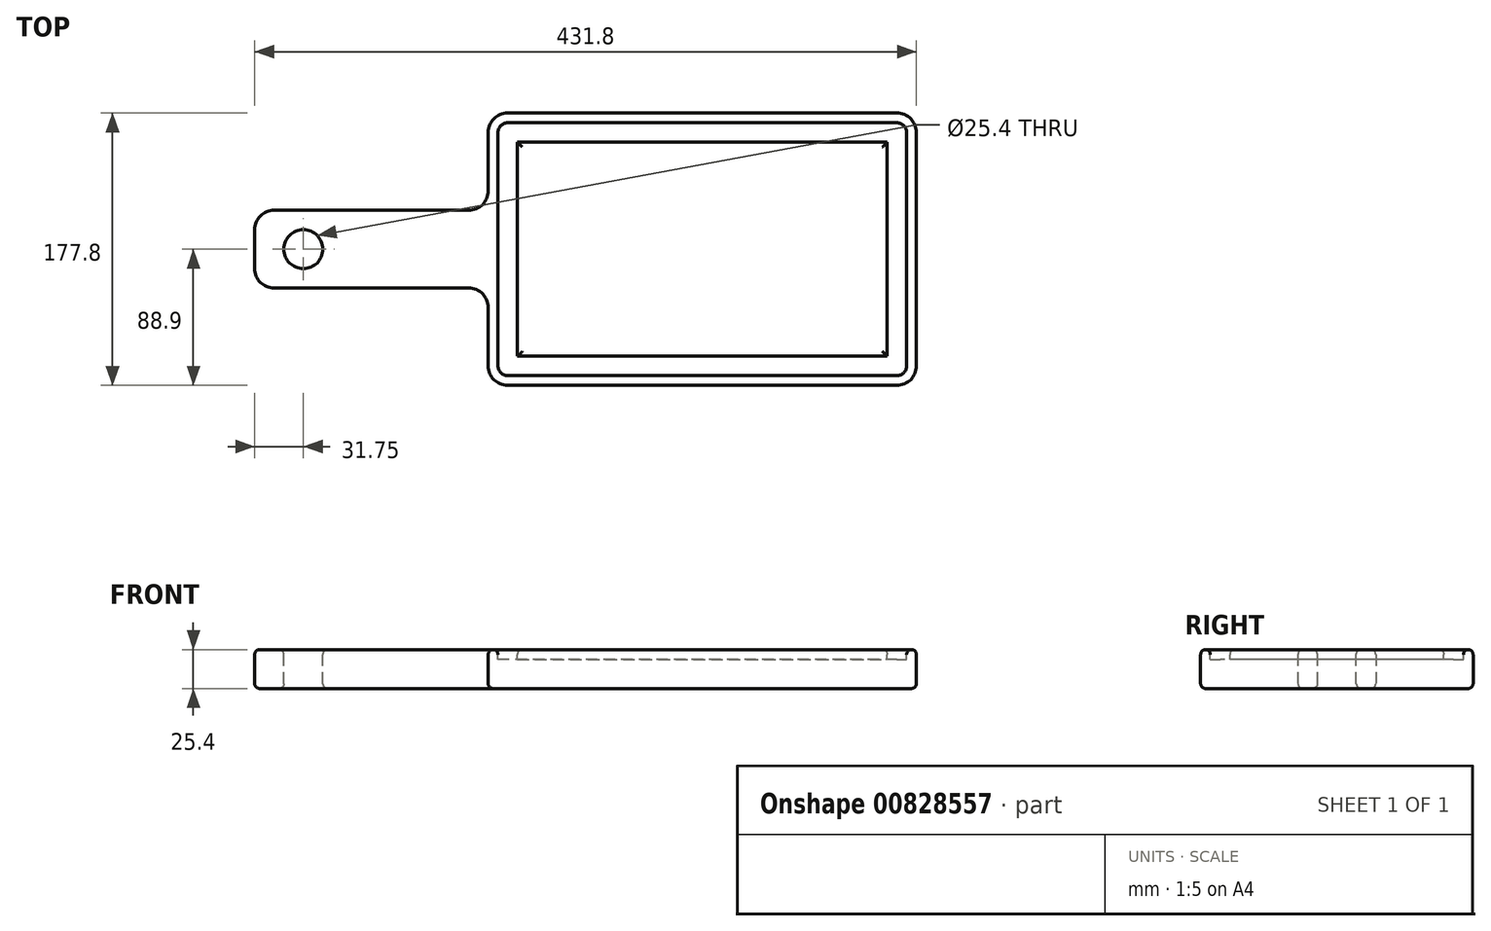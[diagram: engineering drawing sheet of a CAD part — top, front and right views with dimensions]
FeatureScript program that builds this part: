
annotation { "Feature Type Name" : "Feature", "Feature Type Description" : "" }
export const myFeature = defineFeature(function(context is Context, id is Id, definition is map)
    precondition{}
    {
        {
            var Q0;
            Q0=qCreatedBy(makeId("Top.planeOp"),FACE);
            var sketch = newSketch(context, id + "F0", { "sketchPlane" : qUnion([Q0])});
            skLineSegment(sketch, "E0.bottom", {"start": v(0, 0) * mm, "end": v(279.4, 0) * mm});
            skLineSegment(sketch, "E0.top", {"start": v(0, 177.8) * mm, "end": v(279.4, 177.8) * mm});
            skLineSegment(sketch, "E0.left", {"start": v(0, 0) * mm, "end": v(0, 177.8) * mm});
            skLineSegment(sketch, "E0.right", {"start": v(279.4, 0) * mm, "end": v(279.4, 177.8) * mm});
            skLineSegment(sketch, "E1.bottom", {"start": v(0, 114.3) * mm, "end": v(-152.4, 114.3) * mm});
            skLineSegment(sketch, "E1.top", {"start": v(0, 63.5) * mm, "end": v(-152.4, 63.5) * mm});
            skLineSegment(sketch, "E1.left", {"start": v(0, 114.3) * mm, "end": v(0, 63.5) * mm});
            skLineSegment(sketch, "E1.right", {"start": v(-152.4, 114.3) * mm, "end": v(-152.4, 63.5) * mm});
            skSolve(sketch);
        }
        {
            var Q0;
            {var subQ3=sQuery(id+"F0.wireOp",EDGE,"E0.bottom");Q0=makeQuery(id+"F0.imprint","IMPRINT",FACE,{"disambiguationData":[TD([[makeQuery(id+"F0.imprint","IMPRINT",EDGE,{"derivedFrom":subQ3}),1.0]])]});}
            var Q1;
            Q1=makeQuery(id+"F0.imprint","IMPRINT",FACE,{"disambiguationData":[TD([[makeQuery(id+"F0.imprint","IMPRINT",EDGE,{"derivedFrom":sQuery(id+"F0.wireOp",EDGE,"E1.bottom")}),1.0]])]});
            extrude(context, id + "F1", {"entities" : qUnion([Q0, Q1]), "depth" : 25.4 * mm, "offsetDistance" : 25.4 * mm});
        }
        {
            var Q0;
            Q0=makeQuery(id+"F1.opExtrude","CAP_FACE",FACE,{"disambiguationData":[OSD([sQuery(id+"F0.wireOp",EDGE,"E0.bottom"),sQuery(id+"F0.wireOp",EDGE,"E0.top"),sQuery(id+"F0.wireOp",EDGE,"E0.left"),sQuery(id+"F0.wireOp",EDGE,"E0.right"),sQuery(id+"F0.wireOp",EDGE,"E1.bottom"),sQuery(id+"F0.wireOp",EDGE,"E1.top"),sQuery(id+"F0.wireOp",EDGE,"E1.right")])],"isStart":false});
            var sketch = newSketch(context, id + "F2", { "sketchPlane" : qUnion([Q0])});
            skCircle(sketch, "E2", {"center": v(-120.65, 88.9) * mm, "radius": 12.7 * mm});
            skSolve(sketch);
        }
        {
            var Q0;
            Q0 = qSketchRegion(id + "F2", true);
            extrude(context, id + "F3", {"entities" : qUnion([Q0]), "operationType" : NewBodyOperationType.REMOVE, "oppositeDirection" : true, "depth" : 25.4 * mm, "offsetDistance" : 25.4 * mm});
        }
        {
            var Q0;
            Q0=makeQuery(id+"F1.opExtrude","CAP_FACE",FACE,{"disambiguationData":[OSD([sQuery(id+"F0.wireOp",EDGE,"E0.bottom"),sQuery(id+"F0.wireOp",EDGE,"E0.top"),sQuery(id+"F0.wireOp",EDGE,"E0.left"),sQuery(id+"F0.wireOp",EDGE,"E0.right"),sQuery(id+"F0.wireOp",EDGE,"E1.bottom"),sQuery(id+"F0.wireOp",EDGE,"E1.top"),sQuery(id+"F0.wireOp",EDGE,"E1.right")])],"isStart":false});
            var sketch = newSketch(context, id + "F4", { "sketchPlane" : qUnion([Q0])});
            skLineSegment(sketch, "E3.0", {"start": v(6.35, 177.8) * mm, "end": v(279.4, 177.8) * mm});
            skLineSegment(sketch, "E4.0", {"start": v(273.05, 171.45) * mm, "end": v(6.35, 171.45) * mm});
            skLineSegment(sketch, "E4.1", {"start": v(273.05, 6.35) * mm, "end": v(273.05, 171.45) * mm});
            skLineSegment(sketch, "E4.2", {"start": v(6.35, 171.45) * mm, "end": v(6.35, 107.95) * mm});
            skLineSegment(sketch, "E4.3", {"start": v(6.35, 6.35) * mm, "end": v(273.05, 6.35) * mm});
            skLineSegment(sketch, "E4.4", {"start": v(6.35, 107.95) * mm, "end": v(-146.05, 107.95) * mm});
            skLineSegment(sketch, "E4.5", {"start": v(-146.05, 107.95) * mm, "end": v(-146.05, 69.85) * mm});
            skLineSegment(sketch, "E4.6", {"start": v(-146.05, 69.85) * mm, "end": v(6.35, 69.85) * mm});
            skLineSegment(sketch, "E4.7", {"start": v(6.35, 69.85) * mm, "end": v(6.35, 6.35) * mm});
            skLineSegment(sketch, "E5.0", {"start": v(273.05, 184.15) * mm, "end": v(6.35, 184.15) * mm});
            skLineSegment(sketch, "E6", {"start": v(6.35, 107.95) * mm, "end": v(6.35, 69.85) * mm});
            skLineSegment(sketch, "E7.0", {"start": v(19.05, 158.75) * mm, "end": v(19.05, 107.95) * mm});
            skLineSegment(sketch, "E7.1", {"start": v(19.05, 69.85) * mm, "end": v(19.05, 19.05) * mm});
            skLineSegment(sketch, "E7.2", {"start": v(19.05, 19.05) * mm, "end": v(260.35, 19.05) * mm});
            skLineSegment(sketch, "E7.3", {"start": v(260.35, 19.05) * mm, "end": v(260.35, 158.75) * mm});
            skLineSegment(sketch, "E7.4", {"start": v(260.35, 158.75) * mm, "end": v(19.05, 158.75) * mm});
            skLineSegment(sketch, "E8", {"start": v(19.05, 107.95) * mm, "end": v(19.05, 69.85) * mm});
            skSolve(sketch);
        }
        {
            var Q0;
            Q0=makeQuery(id+"F4.imprint","IMPRINT",FACE,{"disambiguationData":[TD([[makeQuery(id+"F4.imprint","IMPRINT",EDGE,{"derivedFrom":sQuery(id+"F4.wireOp",EDGE,"E4.0")}),1.0]])]});
            extrude(context, id + "F5", {"entities" : qUnion([Q0]), "operationType" : NewBodyOperationType.REMOVE, "oppositeDirection" : true, "depth" : 6.35 * mm, "offsetDistance" : 25.4 * mm});
        }
        {
            var Q0;
            Q0=makeQuery(id+"F5.boolean.opBoolean","COPY",EDGE,{"derivedFrom":makeQuery(id+"F5.opExtrude","SWEPT_EDGE",EDGE,{"disambiguationData":[OSD([sQuery(id+"F4.wireOp",EDGE,"E4.0"),sQuery(id+"F4.wireOp",EDGE,"E4.2")])]})});
            var Q1;
            Q1=makeQuery(id+"F5.boolean.opBoolean","COPY",EDGE,{"derivedFrom":makeQuery(id+"F5.opExtrude","SWEPT_EDGE",EDGE,{"disambiguationData":[OSD([sQuery(id+"F4.wireOp",EDGE,"E4.0"),sQuery(id+"F4.wireOp",EDGE,"E4.1")])]})});
            var Q2;
            Q2=makeQuery(id+"F5.boolean.opBoolean","COPY",EDGE,{"derivedFrom":makeQuery(id+"F5.opExtrude","SWEPT_EDGE",EDGE,{"disambiguationData":[OSD([sQuery(id+"F4.wireOp",EDGE,"E4.3"),sQuery(id+"F4.wireOp",EDGE,"E4.7")])]})});
            var Q3;
            Q3=makeQuery(id+"F5.boolean.opBoolean","COPY",EDGE,{"derivedFrom":makeQuery(id+"F5.opExtrude","SWEPT_EDGE",EDGE,{"disambiguationData":[OSD([sQuery(id+"F4.wireOp",EDGE,"E4.1"),sQuery(id+"F4.wireOp",EDGE,"E4.3")])]})});
            fillet(context, id + "F6", {"entities" : qUnion([Q0, Q1, Q2, Q3]), "radius" : 6.35 * mm, "tangentPropagation" : true, "allowEdgeOverflow" : false});
        }
        {
            var Q0;
            Q0=makeQuery(id+"F1.opExtrude","SWEPT_EDGE",EDGE,{"disambiguationData":[OSD([sQuery(id+"F0.wireOp",EDGE,"E0.bottom"),sQuery(id+"F0.wireOp",EDGE,"E0.left")])]});
            var Q1;
            Q1=makeQuery(id+"F1.opExtrude","SWEPT_EDGE",EDGE,{"disambiguationData":[OSD([sQuery(id+"F0.wireOp",EDGE,"E1.top"),sQuery(id+"F0.wireOp",EDGE,"E1.right")])]});
            var Q2;
            Q2=makeQuery(id+"F1.opExtrude","SWEPT_EDGE",EDGE,{"disambiguationData":[OSD([sQuery(id+"F0.wireOp",EDGE,"E0.left"),sQuery(id+"F0.wireOp",EDGE,"E1.top"),sQuery(id+"F0.wireOp",EDGE,"E1.left")])]});
            var Q3;
            Q3=makeQuery(id+"F1.opExtrude","SWEPT_EDGE",EDGE,{"disambiguationData":[OSD([sQuery(id+"F0.wireOp",EDGE,"E1.bottom"),sQuery(id+"F0.wireOp",EDGE,"E1.right")])]});
            var Q4;
            Q4=makeQuery(id+"F1.opExtrude","SWEPT_EDGE",EDGE,{"disambiguationData":[OSD([sQuery(id+"F0.wireOp",EDGE,"E0.left"),sQuery(id+"F0.wireOp",EDGE,"E1.bottom"),sQuery(id+"F0.wireOp",EDGE,"E1.left")])]});
            var Q5;
            Q5=makeQuery(id+"F1.opExtrude","SWEPT_EDGE",EDGE,{"disambiguationData":[OSD([sQuery(id+"F0.wireOp",EDGE,"E0.top"),sQuery(id+"F0.wireOp",EDGE,"E0.left")])]});
            var Q6;
            Q6=makeQuery(id+"F1.opExtrude","SWEPT_EDGE",EDGE,{"disambiguationData":[OSD([sQuery(id+"F0.wireOp",EDGE,"E0.bottom"),sQuery(id+"F0.wireOp",EDGE,"E0.right")])]});
            var Q7;
            Q7=makeQuery(id+"F1.opExtrude","SWEPT_EDGE",EDGE,{"disambiguationData":[OSD([sQuery(id+"F0.wireOp",EDGE,"E0.top"),sQuery(id+"F0.wireOp",EDGE,"E0.right")])]});
            fillet(context, id + "F7", {"entities" : qUnion([Q0, Q1, Q2, Q3, Q4, Q5, Q6, Q7]), "radius" : 12.7 * mm, "tangentPropagation" : true, "allowEdgeOverflow" : false});
        }
        {
            var Q0;
            Q0=makeQuery(id+"F5.boolean.opBoolean","SPLIT",FACE,{"disambiguationData":[TD([makeQuery(id+"F5.opExtrude","SWEPT_FACE",FACE,{"disambiguationData":[OSD([sQuery(id+"F4.wireOp",EDGE,"E7.2")])]})])],"derivedFrom":makeQuery(id+"F1.opExtrude","CAP_FACE",FACE,{"disambiguationData":[OSD([sQuery(id+"F0.wireOp",EDGE,"E0.bottom"),sQuery(id+"F0.wireOp",EDGE,"E0.top"),sQuery(id+"F0.wireOp",EDGE,"E0.left"),sQuery(id+"F0.wireOp",EDGE,"E0.right"),sQuery(id+"F0.wireOp",EDGE,"E1.bottom"),sQuery(id+"F0.wireOp",EDGE,"E1.top"),sQuery(id+"F0.wireOp",EDGE,"E1.right")])],"isStart":false})});
            var Q1;
            {var subQ0=sQuery(id+"F0.wireOp",EDGE,"E1.right");var subQ1=sQuery(id+"F0.wireOp",EDGE,"E1.top");var subQ2=sQuery(id+"F0.wireOp",EDGE,"E1.bottom");var subQ3=sQuery(id+"F0.wireOp",EDGE,"E0.right");var subQ4=sQuery(id+"F0.wireOp",EDGE,"E0.bottom");var subQ5=sQuery(id+"F0.wireOp",EDGE,"E0.left");var subQ6=sQuery(id+"F0.wireOp",EDGE,"E0.top");Q1=makeQuery(id+"F5.boolean.opBoolean","SPLIT",FACE,{"disambiguationData":[TD([makeQuery(id+"F1.opExtrude","SWEPT_FACE",FACE,{"disambiguationData":[OSD([subQ4])]})])],"derivedFrom":makeQuery(id+"F1.opExtrude","CAP_FACE",FACE,{"disambiguationData":[OSD([subQ4,subQ6,subQ5,subQ3,subQ2,subQ1,subQ0])],"isStart":false})});}
            var Q2;
            Q2=makeQuery(id+"F1.opExtrude","CAP_FACE",FACE,{"disambiguationData":[OSD([sQuery(id+"F0.wireOp",EDGE,"E0.bottom"),sQuery(id+"F0.wireOp",EDGE,"E0.top"),sQuery(id+"F0.wireOp",EDGE,"E0.left"),sQuery(id+"F0.wireOp",EDGE,"E0.right"),sQuery(id+"F0.wireOp",EDGE,"E1.bottom"),sQuery(id+"F0.wireOp",EDGE,"E1.top"),sQuery(id+"F0.wireOp",EDGE,"E1.right")])],"isStart":true});
            fillet(context, id + "F8", {"entities" : qUnion([Q0, Q1, Q2]), "radius" : 3.17 * mm, "tangentPropagation" : true, "allowEdgeOverflow" : false});
        }
    });
